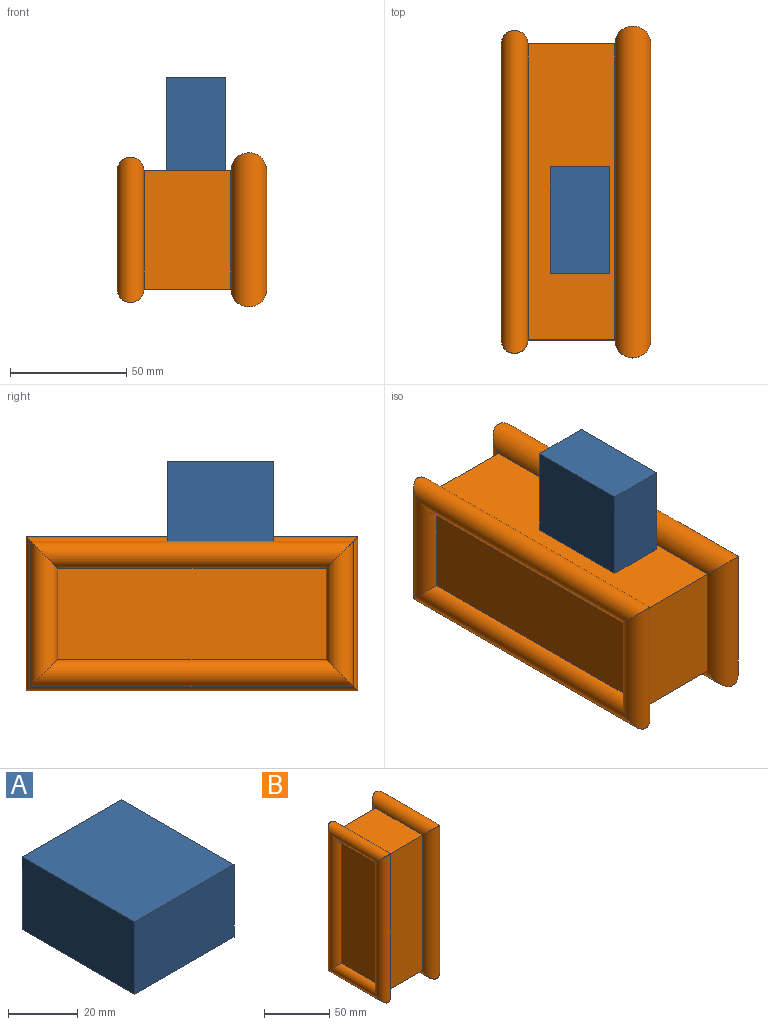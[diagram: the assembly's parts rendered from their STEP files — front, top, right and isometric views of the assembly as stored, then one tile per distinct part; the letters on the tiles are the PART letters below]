
ASSEMBLY  parts=2 mates=1
PART A: 6 faces, bbox 40.2x45.6x25.4 mm
  f0: plane 45.62x25.4mm, normal (1,0,0), area 1158.8mm2, adj f1,f3,f4,f5
  f1: plane 40.22x25.4mm, normal (0,1,0), area 1021.5mm2, adj f0,f2,f4,f5
  f2: plane 45.62x25.4mm, normal (-1,0,0), area 1158.8mm2, adj f1,f3,f4,f5
  f3: plane 40.22x25.4mm, normal (0,-1,0), area 1021.5mm2, adj f0,f2,f4,f5
  f4: plane 45.62x40.22mm, normal (0,0,1), area 1834.8mm2, adj f0,f1,f2,f3
  f5: plane 45.62x40.22mm, normal (0,0,-1), area 1834.8mm2, adj f0,f1,f2,f3
PART B: 14 faces, bbox 64.3x66.3x142.5 mm
  f0: plane 127x37.32mm, normal (0,1,0), area 4739.9mm2, adj f2,f3,f5,f12
  f1: plane 127x37.32mm, normal (0,-1,0), area 4739.9mm2, adj f2,f3,f4,f11
  f2: plane 50.8x37.32mm, normal (0,0,1), area 1896mm2, adj f0,f1,f7,f9
  f3: plane 50.8x37.32mm, normal (0,0,-1), area 1896mm2, adj f0,f1,f6,f10
  f4: cylinder r=7.7mm len=142.48mm, axis (0,0,1), area 4726.6mm2, adj f1,f6,f7,f8
  f5: cylinder r=7.7mm len=142.48mm, axis (0,0,-1), area 4726.6mm2, adj f0,f6,f7,f8
  f6: cylinder r=7.7mm len=66.28mm, axis (0,-1,0), area 1961.8mm2, adj f3,f4,f5,f8
  f7: cylinder r=7.7mm len=66.28mm, axis (0,1,0), area 1961.8mm2, adj f2,f4,f5,f8
  f8: plane 111.6x35.4mm, normal (1,0,0), area 3950.7mm2, adj f4,f5,f6,f7
  f9: cylinder r=5.78mm len=62.42mm, axis (0,1,0), area 1450mm2, adj f2,f11,f12,f13
  f10: cylinder r=5.78mm len=62.42mm, axis (0,-1,0), area 1450mm2, adj f3,f11,f12,f13
  f11: cylinder r=5.78mm len=138.62mm, axis (0,0,1), area 3524.8mm2, adj f1,f9,f10,f13
  f12: cylinder r=5.78mm len=138.62mm, axis (0,0,-1), area 3524.8mm2, adj f0,f9,f10,f13
  f13: plane 115.44x39.24mm, normal (-1,0,0), area 4530.5mm2, adj f9,f10,f11,f12
PLACE A rot(axis=(-0.71,0,0.71),180deg) t=(-190.89,25.51,446.53)mm
PLACE B rot(axis=(1,0,0),90deg) t=(-180.81,100.42,309.41)mm
MATE planar A.f0 <-> B.f0  axis (0,0,-1) through (-203.59,24.75,360.21)mm
